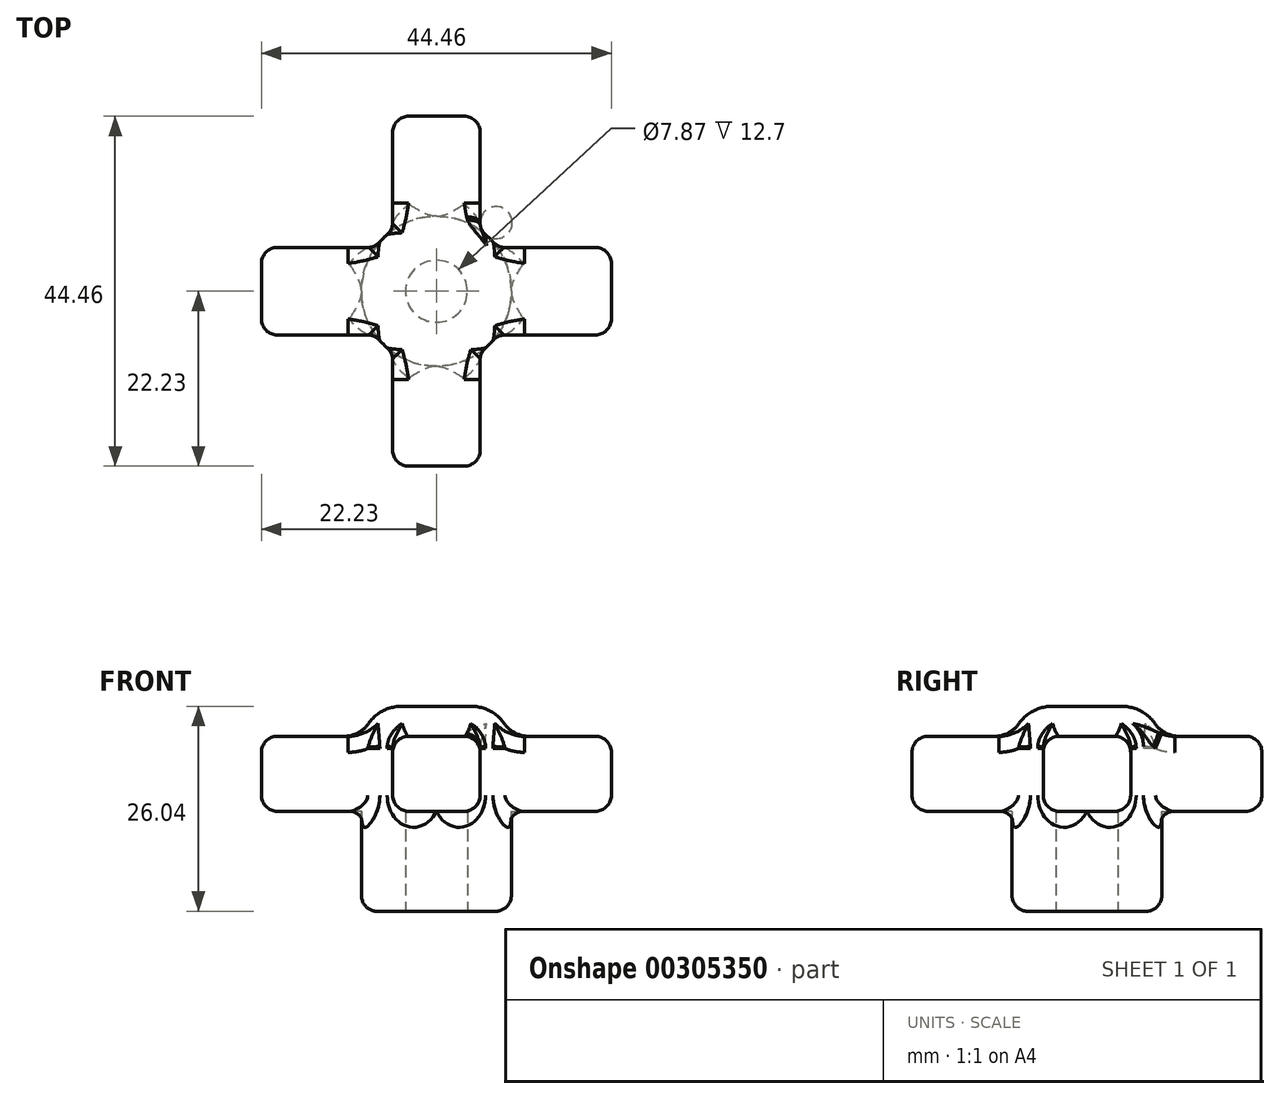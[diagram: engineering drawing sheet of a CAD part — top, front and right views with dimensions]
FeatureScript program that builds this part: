
annotation { "Feature Type Name" : "Feature", "Feature Type Description" : "" }
export const myFeature = defineFeature(function(context is Context, id is Id, definition is map)
    precondition{}
    {
        {
            var Q0;
            Q0=qCreatedBy(makeId("Top.planeOp"),FACE);
            var sketch = newSketch(context, id + "F0", { "sketchPlane" : qUnion([Q0])});
            skCircle(sketch, "E0", {"center": v(0, 0) * mm, "radius": 9.53 * mm});
            skSolve(sketch);
        }
        {
            var Q0;
            Q0=makeQuery(id+"F0.imprint","IMPRINT",FACE,{"disambiguationData":[TD([[makeQuery(id+"F0.imprint","IMPRINT",EDGE,{"derivedFrom":sQuery(id+"F0.wireOp",EDGE,"E0")}),1.0]])]});
            extrude(context, id + "F1", {"entities" : qUnion([Q0]), "depth" : 12.7 * mm});
        }
        {
            var Q0;
            Q0=makeQuery(id+"F1.opExtrude","CAP_FACE",FACE,{"disambiguationData":[OSD([sQuery(id+"F0.wireOp",EDGE,"E0")])],"isStart":false});
            var sketch = newSketch(context, id + "F2", { "sketchPlane" : qUnion([Q0])});
            skLineSegment(sketch, "E1.bottom", {"start": v(-5.56, 22.23) * mm, "end": v(5.56, 22.23) * mm});
            skLineSegment(sketch, "E1.top", {"start": v(-5.56, -22.23) * mm, "end": v(5.56, -22.23) * mm});
            skLineSegment(sketch, "E1.left", {"start": v(-5.56, 22.23) * mm, "end": v(-5.56, -22.23) * mm});
            skLineSegment(sketch, "E1.right", {"start": v(5.56, 22.23) * mm, "end": v(5.56, -22.23) * mm});
            skPoint(sketch, "E1.middle", {"position": v(0, 0) * mm});
            skLineSegment(sketch, "E2.bottom", {"start": v(22.23, 5.56) * mm, "end": v(-22.23, 5.56) * mm});
            skLineSegment(sketch, "E2.top", {"start": v(22.23, -5.56) * mm, "end": v(-22.23, -5.56) * mm});
            skLineSegment(sketch, "E2.left", {"start": v(22.23, 5.56) * mm, "end": v(22.23, -5.56) * mm});
            skLineSegment(sketch, "E2.right", {"start": v(-22.23, 5.56) * mm, "end": v(-22.23, -5.56) * mm});
            skSolve(sketch);
        }
        {
            var Q0;
            {var subQ0=sQuery(id+"F2.wireOp",EDGE,"E1.bottom");Q0=makeQuery(id+"F2.imprint","IMPRINT",FACE,{"disambiguationData":[TD([[makeQuery(id+"F2.imprint","IMPRINT",EDGE,{"derivedFrom":subQ0}),-1.0]])]});}
            var Q1;
            {var subQ0=sQuery(id+"F2.wireOp",EDGE,"E2.left");Q1=makeQuery(id+"F2.imprint","IMPRINT",FACE,{"disambiguationData":[TD([[makeQuery(id+"F2.imprint","IMPRINT",EDGE,{"derivedFrom":subQ0}),-1.0]])]});}
            var Q2;
            {var subQ0=sQuery(id+"F2.wireOp",EDGE,"E2.bottom");var subQ1=sQuery(id+"F2.wireOp",EDGE,"E1.left");var subQ2=makeQuery(id+"F2.imprint","INTERSECT",VERTEX,{"derivedFrom":[subQ1,subQ0]});Q2=makeQuery(id+"F2.imprint","IMPRINT",FACE,{"disambiguationData":[TD([[makeQuery(id+"F2.imprint","IMPRINT",EDGE,{"disambiguationData":[TD([[subQ2,-1.0]])],"derivedFrom":subQ1}),1.0]])]});}
            var Q3;
            {var subQ0=sQuery(id+"F2.wireOp",EDGE,"E2.bottom");var subQ1=sQuery(id+"F2.wireOp",EDGE,"E1.left");var subQ2=makeQuery(id+"F2.imprint","INTERSECT",VERTEX,{"derivedFrom":[subQ1,subQ0]});Q3=makeQuery(id+"F2.imprint","IMPRINT",FACE,{"disambiguationData":[TD([[makeQuery(id+"F2.imprint","IMPRINT",EDGE,{"disambiguationData":[TD([[subQ2,1.0]])],"derivedFrom":subQ1}),1.0]])]});}
            var Q4;
            {var subQ0=sQuery(id+"F2.wireOp",EDGE,"E2.bottom");var subQ1=sQuery(id+"F2.wireOp",EDGE,"E1.right");var subQ2=makeQuery(id+"F2.imprint","INTERSECT",VERTEX,{"derivedFrom":[subQ1,subQ0]});Q4=makeQuery(id+"F2.imprint","IMPRINT",FACE,{"disambiguationData":[TD([[makeQuery(id+"F2.imprint","IMPRINT",EDGE,{"disambiguationData":[TD([[subQ2,-1.0]])],"derivedFrom":subQ1}),1.0]])]});}
            var Q5;
            {var subQ0=sQuery(id+"F2.wireOp",EDGE,"E2.top");var subQ1=sQuery(id+"F2.wireOp",EDGE,"E1.left");var subQ2=makeQuery(id+"F2.imprint","INTERSECT",VERTEX,{"derivedFrom":[subQ1,subQ0]});Q5=makeQuery(id+"F2.imprint","IMPRINT",FACE,{"disambiguationData":[TD([[makeQuery(id+"F2.imprint","IMPRINT",EDGE,{"disambiguationData":[TD([[subQ2,-1.0]])],"derivedFrom":subQ1}),1.0]])]});}
            var Q6;
            {var subQ0=sQuery(id+"F2.wireOp",EDGE,"E1.top");Q6=makeQuery(id+"F2.imprint","IMPRINT",FACE,{"disambiguationData":[TD([[makeQuery(id+"F2.imprint","IMPRINT",EDGE,{"derivedFrom":subQ0}),1.0]])]});}
            var Q7;
            {var subQ0=sQuery(id+"F2.wireOp",EDGE,"E2.right");Q7=makeQuery(id+"F2.imprint","IMPRINT",FACE,{"disambiguationData":[TD([[makeQuery(id+"F2.imprint","IMPRINT",EDGE,{"derivedFrom":subQ0}),1.0]])]});}
            var Q8;
            {var subQ0=sQuery(id+"F2.wireOp",EDGE,"E2.bottom");var subQ1=sQuery(id+"F2.wireOp",EDGE,"E1.left");var subQ2=makeQuery(id+"F2.imprint","INTERSECT",VERTEX,{"derivedFrom":[subQ1,subQ0]});Q8=makeQuery(id+"F2.imprint","IMPRINT",FACE,{"disambiguationData":[TD([[makeQuery(id+"F2.imprint","IMPRINT",EDGE,{"disambiguationData":[TD([[subQ2,-1.0]])],"derivedFrom":subQ1}),-1.0]])]});}
            var Q9;
            {var subQ0=sQuery(id+"F2.wireOp",EDGE,"E2.top");var subQ1=sQuery(id+"F2.wireOp",EDGE,"E1.right");var subQ2=makeQuery(id+"F2.imprint","INTERSECT",VERTEX,{"derivedFrom":[subQ1,subQ0]});Q9=makeQuery(id+"F2.imprint","IMPRINT",FACE,{"disambiguationData":[TD([[makeQuery(id+"F2.imprint","IMPRINT",EDGE,{"disambiguationData":[TD([[subQ2,-1.0]])],"derivedFrom":subQ1}),1.0]])]});}
            var Q10;
            {var subQ0=sQuery(id+"F2.wireOp",EDGE,"E2.top");var subQ1=sQuery(id+"F2.wireOp",EDGE,"E1.left");var subQ2=makeQuery(id+"F2.imprint","INTERSECT",VERTEX,{"derivedFrom":[subQ1,subQ0]});Q10=makeQuery(id+"F2.imprint","IMPRINT",FACE,{"disambiguationData":[TD([[makeQuery(id+"F2.imprint","IMPRINT",EDGE,{"disambiguationData":[TD([[subQ2,-1.0]])],"derivedFrom":subQ1}),-1.0]])]});}
            var Q11;
            {var subQ0=sQuery(id+"F2.wireOp",EDGE,"E2.bottom");var subQ1=sQuery(id+"F2.wireOp",EDGE,"E1.right");var subQ2=makeQuery(id+"F2.imprint","INTERSECT",VERTEX,{"derivedFrom":[subQ1,subQ0]});Q11=makeQuery(id+"F2.imprint","IMPRINT",FACE,{"disambiguationData":[TD([[makeQuery(id+"F2.imprint","IMPRINT",EDGE,{"disambiguationData":[TD([[subQ2,1.0]])],"derivedFrom":subQ1}),1.0]])]});}
            var Q12;
            {var subQ0=sQuery(id+"F2.wireOp",EDGE,"E2.bottom");var subQ1=sQuery(id+"F2.wireOp",EDGE,"E1.left");var subQ2=makeQuery(id+"F2.imprint","INTERSECT",VERTEX,{"derivedFrom":[subQ1,subQ0]});Q12=makeQuery(id+"F2.imprint","IMPRINT",FACE,{"disambiguationData":[TD([[makeQuery(id+"F2.imprint","IMPRINT",EDGE,{"disambiguationData":[TD([[subQ2,1.0]])],"derivedFrom":subQ1}),-1.0]])]});}
            extrude(context, id + "F3", {"entities" : qUnion([Q0, Q1, Q2, Q3, Q4, Q5, Q6, Q7, Q8, Q9, Q10, Q11, Q12]), "operationType" : NewBodyOperationType.ADD, "depth" : 9.52 * mm});
        }
        {
            var Q0;
            Q0=makeQuery(id+"F3.opExtrude","CAP_FACE",FACE,{"disambiguationData":[OSD([sQuery(id+"F0.wireOp",EDGE,"E0"),sQuery(id+"F2.wireOp",EDGE,"E1.bottom"),sQuery(id+"F2.wireOp",EDGE,"E1.top"),sQuery(id+"F2.wireOp",EDGE,"E1.left"),sQuery(id+"F2.wireOp",EDGE,"E1.right"),sQuery(id+"F2.wireOp",EDGE,"E2.bottom"),sQuery(id+"F2.wireOp",EDGE,"E2.top"),sQuery(id+"F2.wireOp",EDGE,"E2.left"),sQuery(id+"F2.wireOp",EDGE,"E2.right")])],"isStart":false});
            var sketch = newSketch(context, id + "F4", { "sketchPlane" : qUnion([Q0])});
            skCircle(sketch, "E3", {"center": v(0, 0) * mm, "radius": 9.53 * mm});
            skSolve(sketch);
        }
        {
            var Q0;
            Q0=makeQuery(id+"F4.imprint","IMPRINT",FACE,{"disambiguationData":[TD([[makeQuery(id+"F4.imprint","IMPRINT",EDGE,{"derivedFrom":sQuery(id+"F4.wireOp",EDGE,"E3")}),1.0]])]});
            extrude(context, id + "F5", {"entities" : qUnion([Q0]), "operationType" : NewBodyOperationType.ADD, "depth" : 3.8 * mm});
        }
        {
            var Q0;
            Q0=makeQuery(id+"F5.opExtrude","CAP_EDGE",EDGE,{"disambiguationData":[OSD([sQuery(id+"F4.wireOp",EDGE,"E3")])],"isStart":false});
            fillet(context, id + "F6", {"entities" : qUnion([Q0]), "radius" : 5.08 * mm, "tangentPropagation" : true, "allowEdgeOverflow" : false});
        }
        {
            var Q0;
            {var subQ0=sQuery(id+"F2.wireOp",EDGE,"E2.left");var subQ1=sQuery(id+"F2.wireOp",EDGE,"E2.top");var subQ2=sQuery(id+"F0.wireOp",EDGE,"E0");var subQ5=sQuery(id+"F2.wireOp",EDGE,"E2.bottom");var subQ7=sQuery(id+"F2.wireOp",EDGE,"E1.left");var subQ8=sQuery(id+"F2.wireOp",EDGE,"E1.right");var subQ9=sQuery(id+"F4.wireOp",EDGE,"E3");Q0=makeQuery(id+"F6.opFillet","BLEND_EDGE",EDGE,{"blendedFrom":[makeQuery(id+"F5.opExtrude","CAP_EDGE",EDGE,{"disambiguationData":[OSD([subQ9])],"isStart":false}),makeQuery(id+"F5.boolean.opBoolean","SPLIT",FACE,{"disambiguationData":[TD([makeQuery(id+"F3.opExtrude","SWEPT_FACE",FACE,{"disambiguationData":[OSD([subQ0])]})])],"derivedFrom":makeQuery(id+"F3.opExtrude","CAP_FACE",FACE,{"disambiguationData":[OSD([subQ2,sQuery(id+"F2.wireOp",EDGE,"E1.bottom"),sQuery(id+"F2.wireOp",EDGE,"E1.top"),subQ7,subQ8,subQ5,subQ1,subQ0,sQuery(id+"F2.wireOp",EDGE,"E2.right")])],"isStart":false})})],"blendedInto":[makeQuery(id+"F5.boolean.opBoolean","SPLIT",FACE,{"disambiguationData":[TD([makeQuery(id+"F3.opExtrude","SWEPT_FACE",FACE,{"disambiguationData":[OSD([subQ0])]})])],"derivedFrom":makeQuery(id+"F3.opExtrude","CAP_FACE",FACE,{"disambiguationData":[OSD([subQ2,sQuery(id+"F2.wireOp",EDGE,"E1.bottom"),sQuery(id+"F2.wireOp",EDGE,"E1.top"),subQ7,subQ8,subQ5,subQ1,subQ0,sQuery(id+"F2.wireOp",EDGE,"E2.right")])],"isStart":false})})]});}
            var Q1;
            {var subQ0=sQuery(id+"F2.wireOp",EDGE,"E1.right");var subQ1=sQuery(id+"F2.wireOp",EDGE,"E1.bottom");var subQ2=sQuery(id+"F0.wireOp",EDGE,"E0");var subQ5=sQuery(id+"F2.wireOp",EDGE,"E2.top");var subQ6=sQuery(id+"F2.wireOp",EDGE,"E1.left");var subQ8=sQuery(id+"F2.wireOp",EDGE,"E2.bottom");var subQ9=sQuery(id+"F4.wireOp",EDGE,"E3");Q1=makeQuery(id+"F6.opFillet","BLEND_EDGE",EDGE,{"blendedFrom":[makeQuery(id+"F5.opExtrude","CAP_EDGE",EDGE,{"disambiguationData":[OSD([subQ9])],"isStart":false}),makeQuery(id+"F5.boolean.opBoolean","SPLIT",FACE,{"disambiguationData":[TD([makeQuery(id+"F3.opExtrude","SWEPT_FACE",FACE,{"disambiguationData":[OSD([subQ1])]})])],"derivedFrom":makeQuery(id+"F3.opExtrude","CAP_FACE",FACE,{"disambiguationData":[OSD([subQ2,subQ1,sQuery(id+"F2.wireOp",EDGE,"E1.top"),subQ6,subQ0,subQ8,subQ5,sQuery(id+"F2.wireOp",EDGE,"E2.left"),sQuery(id+"F2.wireOp",EDGE,"E2.right")])],"isStart":false})})],"blendedInto":[makeQuery(id+"F5.boolean.opBoolean","SPLIT",FACE,{"disambiguationData":[TD([makeQuery(id+"F3.opExtrude","SWEPT_FACE",FACE,{"disambiguationData":[OSD([subQ1])]})])],"derivedFrom":makeQuery(id+"F3.opExtrude","CAP_FACE",FACE,{"disambiguationData":[OSD([subQ2,subQ1,sQuery(id+"F2.wireOp",EDGE,"E1.top"),subQ6,subQ0,subQ8,subQ5,sQuery(id+"F2.wireOp",EDGE,"E2.left"),sQuery(id+"F2.wireOp",EDGE,"E2.right")])],"isStart":false})})]});}
            var Q2;
            {var subQ0=sQuery(id+"F2.wireOp",EDGE,"E2.right");var subQ1=sQuery(id+"F2.wireOp",EDGE,"E2.top");var subQ2=sQuery(id+"F0.wireOp",EDGE,"E0");var subQ5=sQuery(id+"F2.wireOp",EDGE,"E2.bottom");var subQ7=sQuery(id+"F2.wireOp",EDGE,"E1.left");var subQ8=sQuery(id+"F2.wireOp",EDGE,"E1.right");var subQ9=sQuery(id+"F4.wireOp",EDGE,"E3");Q2=makeQuery(id+"F6.opFillet","BLEND_EDGE",EDGE,{"blendedFrom":[makeQuery(id+"F5.opExtrude","CAP_EDGE",EDGE,{"disambiguationData":[OSD([subQ9])],"isStart":false}),makeQuery(id+"F5.boolean.opBoolean","SPLIT",FACE,{"disambiguationData":[TD([makeQuery(id+"F3.opExtrude","SWEPT_FACE",FACE,{"disambiguationData":[OSD([subQ0])]})])],"derivedFrom":makeQuery(id+"F3.opExtrude","CAP_FACE",FACE,{"disambiguationData":[OSD([subQ2,sQuery(id+"F2.wireOp",EDGE,"E1.bottom"),sQuery(id+"F2.wireOp",EDGE,"E1.top"),subQ7,subQ8,subQ5,subQ1,sQuery(id+"F2.wireOp",EDGE,"E2.left"),subQ0])],"isStart":false})})],"blendedInto":[makeQuery(id+"F5.boolean.opBoolean","SPLIT",FACE,{"disambiguationData":[TD([makeQuery(id+"F3.opExtrude","SWEPT_FACE",FACE,{"disambiguationData":[OSD([subQ0])]})])],"derivedFrom":makeQuery(id+"F3.opExtrude","CAP_FACE",FACE,{"disambiguationData":[OSD([subQ2,sQuery(id+"F2.wireOp",EDGE,"E1.bottom"),sQuery(id+"F2.wireOp",EDGE,"E1.top"),subQ7,subQ8,subQ5,subQ1,sQuery(id+"F2.wireOp",EDGE,"E2.left"),subQ0])],"isStart":false})})]});}
            var Q3;
            {var subQ0=sQuery(id+"F2.wireOp",EDGE,"E1.left");var subQ1=sQuery(id+"F2.wireOp",EDGE,"E1.top");var subQ2=sQuery(id+"F0.wireOp",EDGE,"E0");var subQ5=sQuery(id+"F2.wireOp",EDGE,"E1.right");var subQ6=sQuery(id+"F2.wireOp",EDGE,"E2.bottom");var subQ7=sQuery(id+"F4.wireOp",EDGE,"E3");var subQ9=sQuery(id+"F2.wireOp",EDGE,"E2.top");Q3=makeQuery(id+"F6.opFillet","BLEND_EDGE",EDGE,{"blendedFrom":[makeQuery(id+"F5.opExtrude","CAP_EDGE",EDGE,{"disambiguationData":[OSD([subQ7])],"isStart":false}),makeQuery(id+"F5.boolean.opBoolean","SPLIT",FACE,{"disambiguationData":[TD([makeQuery(id+"F3.opExtrude","SWEPT_FACE",FACE,{"disambiguationData":[OSD([subQ1])]})])],"derivedFrom":makeQuery(id+"F3.opExtrude","CAP_FACE",FACE,{"disambiguationData":[OSD([subQ2,sQuery(id+"F2.wireOp",EDGE,"E1.bottom"),subQ1,subQ0,subQ5,subQ6,subQ9,sQuery(id+"F2.wireOp",EDGE,"E2.left"),sQuery(id+"F2.wireOp",EDGE,"E2.right")])],"isStart":false})})],"blendedInto":[makeQuery(id+"F5.boolean.opBoolean","SPLIT",FACE,{"disambiguationData":[TD([makeQuery(id+"F3.opExtrude","SWEPT_FACE",FACE,{"disambiguationData":[OSD([subQ1])]})])],"derivedFrom":makeQuery(id+"F3.opExtrude","CAP_FACE",FACE,{"disambiguationData":[OSD([subQ2,sQuery(id+"F2.wireOp",EDGE,"E1.bottom"),subQ1,subQ0,subQ5,subQ6,subQ9,sQuery(id+"F2.wireOp",EDGE,"E2.left"),sQuery(id+"F2.wireOp",EDGE,"E2.right")])],"isStart":false})})]});}
            fillet(context, id + "F7", {"entities" : qUnion([Q0, Q1, Q2, Q3]), "radius" : 3.8 * mm, "tangentPropagation" : true, "allowEdgeOverflow" : false});
        }
        {
            var Q0;
            Q0=makeQuery(id+"F3.opExtrude","CAP_EDGE",EDGE,{"disambiguationData":[OSD([sQuery(id+"F2.wireOp",EDGE,"E2.left")])],"isStart":false});
            var Q1;
            {var subQ0=sQuery(id+"F2.wireOp",EDGE,"E2.bottom");Q1=makeQuery(id+"F3.opExtrude","CAP_EDGE",EDGE,{"disambiguationData":[OSD([subQ0]),TDD([makeQuery(id+"F2.imprint","IMPRINT",EDGE,{"disambiguationData":[TD([[makeQuery(id+"F2.imprint","INTERSECT",VERTEX,{"derivedFrom":[subQ0,sQuery(id+"F2.wireOp",EDGE,"E2.left")]}),-1.0]])],"derivedFrom":subQ0})])],"isStart":false});}
            var Q2;
            {var subQ0=sQuery(id+"F2.wireOp",EDGE,"E2.top");Q2=makeQuery(id+"F3.opExtrude","CAP_EDGE",EDGE,{"disambiguationData":[OSD([subQ0]),TDD([makeQuery(id+"F2.imprint","IMPRINT",EDGE,{"disambiguationData":[TD([[makeQuery(id+"F2.imprint","INTERSECT",VERTEX,{"derivedFrom":[subQ0,sQuery(id+"F2.wireOp",EDGE,"E2.left")]}),-1.0]])],"derivedFrom":subQ0})])],"isStart":false});}
            var Q3;
            {var subQ0=sQuery(id+"F2.wireOp",EDGE,"E2.top");Q3=makeQuery(id+"F3.opExtrude","CAP_EDGE",EDGE,{"disambiguationData":[OSD([subQ0]),TDD([makeQuery(id+"F2.imprint","IMPRINT",EDGE,{"disambiguationData":[TD([[makeQuery(id+"F2.imprint","INTERSECT",VERTEX,{"derivedFrom":[subQ0,sQuery(id+"F2.wireOp",EDGE,"E2.left")]}),-1.0]])],"derivedFrom":subQ0})])],"isStart":true});}
            var Q4;
            Q4=makeQuery(id+"F3.opExtrude","CAP_EDGE",EDGE,{"disambiguationData":[OSD([sQuery(id+"F2.wireOp",EDGE,"E2.left")])],"isStart":true});
            var Q5;
            Q5=makeQuery(id+"F3.opExtrude","SWEPT_EDGE",EDGE,{"disambiguationData":[OSD([sQuery(id+"F2.wireOp",EDGE,"E2.top"),sQuery(id+"F2.wireOp",EDGE,"E2.left")])]});
            var Q6;
            Q6=makeQuery(id+"F3.opExtrude","SWEPT_EDGE",EDGE,{"disambiguationData":[OSD([sQuery(id+"F2.wireOp",EDGE,"E2.bottom"),sQuery(id+"F2.wireOp",EDGE,"E2.left")])]});
            var Q7;
            {var subQ0=sQuery(id+"F2.wireOp",EDGE,"E2.bottom");Q7=makeQuery(id+"F3.opExtrude","CAP_EDGE",EDGE,{"disambiguationData":[OSD([subQ0]),TDD([makeQuery(id+"F2.imprint","IMPRINT",EDGE,{"disambiguationData":[TD([[makeQuery(id+"F2.imprint","INTERSECT",VERTEX,{"derivedFrom":[subQ0,sQuery(id+"F2.wireOp",EDGE,"E2.left")]}),-1.0]])],"derivedFrom":subQ0})])],"isStart":true});}
            var Q8;
            {var subQ0=sQuery(id+"F2.wireOp",EDGE,"E1.right");Q8=makeQuery(id+"F3.opExtrude","CAP_EDGE",EDGE,{"disambiguationData":[OSD([subQ0]),TDD([makeQuery(id+"F2.imprint","IMPRINT",EDGE,{"disambiguationData":[TD([[makeQuery(id+"F2.imprint","INTERSECT",VERTEX,{"derivedFrom":[sQuery(id+"F2.wireOp",EDGE,"E1.bottom"),subQ0]}),-1.0]])],"derivedFrom":subQ0})])],"isStart":true});}
            var Q9;
            Q9=makeQuery(id+"F3.opExtrude","SWEPT_EDGE",EDGE,{"disambiguationData":[OSD([sQuery(id+"F2.wireOp",EDGE,"E1.bottom"),sQuery(id+"F2.wireOp",EDGE,"E1.right")])]});
            var Q10;
            Q10=makeQuery(id+"F3.opExtrude","CAP_EDGE",EDGE,{"disambiguationData":[OSD([sQuery(id+"F2.wireOp",EDGE,"E1.bottom")])],"isStart":false});
            var Q11;
            Q11=makeQuery(id+"F3.opExtrude","CAP_EDGE",EDGE,{"disambiguationData":[OSD([sQuery(id+"F2.wireOp",EDGE,"E1.bottom")])],"isStart":true});
            var Q12;
            Q12=makeQuery(id+"F3.opExtrude","SWEPT_EDGE",EDGE,{"disambiguationData":[OSD([sQuery(id+"F2.wireOp",EDGE,"E1.bottom"),sQuery(id+"F2.wireOp",EDGE,"E1.left")])]});
            var Q13;
            {var subQ0=sQuery(id+"F2.wireOp",EDGE,"E1.left");Q13=makeQuery(id+"F3.opExtrude","CAP_EDGE",EDGE,{"disambiguationData":[OSD([subQ0]),TDD([makeQuery(id+"F2.imprint","IMPRINT",EDGE,{"disambiguationData":[TD([[makeQuery(id+"F2.imprint","INTERSECT",VERTEX,{"derivedFrom":[sQuery(id+"F2.wireOp",EDGE,"E1.bottom"),subQ0]}),-1.0]])],"derivedFrom":subQ0})])],"isStart":false});}
            var Q14;
            {var subQ0=sQuery(id+"F2.wireOp",EDGE,"E1.left");Q14=makeQuery(id+"F3.opExtrude","CAP_EDGE",EDGE,{"disambiguationData":[OSD([subQ0]),TDD([makeQuery(id+"F2.imprint","IMPRINT",EDGE,{"disambiguationData":[TD([[makeQuery(id+"F2.imprint","INTERSECT",VERTEX,{"derivedFrom":[sQuery(id+"F2.wireOp",EDGE,"E1.bottom"),subQ0]}),-1.0]])],"derivedFrom":subQ0})])],"isStart":true});}
            var Q15;
            {var subQ0=sQuery(id+"F2.wireOp",EDGE,"E2.bottom");Q15=makeQuery(id+"F3.opExtrude","CAP_EDGE",EDGE,{"disambiguationData":[OSD([subQ0]),TDD([makeQuery(id+"F2.imprint","IMPRINT",EDGE,{"disambiguationData":[TD([[makeQuery(id+"F2.imprint","INTERSECT",VERTEX,{"derivedFrom":[subQ0,sQuery(id+"F2.wireOp",EDGE,"E2.right")]}),1.0]])],"derivedFrom":subQ0})])],"isStart":false});}
            var Q16;
            Q16=makeQuery(id+"F3.opExtrude","SWEPT_EDGE",EDGE,{"disambiguationData":[OSD([sQuery(id+"F2.wireOp",EDGE,"E2.bottom"),sQuery(id+"F2.wireOp",EDGE,"E2.right")])]});
            var Q17;
            {var subQ0=sQuery(id+"F2.wireOp",EDGE,"E2.bottom");Q17=makeQuery(id+"F3.opExtrude","CAP_EDGE",EDGE,{"disambiguationData":[OSD([subQ0]),TDD([makeQuery(id+"F2.imprint","IMPRINT",EDGE,{"disambiguationData":[TD([[makeQuery(id+"F2.imprint","INTERSECT",VERTEX,{"derivedFrom":[subQ0,sQuery(id+"F2.wireOp",EDGE,"E2.right")]}),1.0]])],"derivedFrom":subQ0})])],"isStart":true});}
            var Q18;
            Q18=makeQuery(id+"F3.opExtrude","CAP_EDGE",EDGE,{"disambiguationData":[OSD([sQuery(id+"F2.wireOp",EDGE,"E2.right")])],"isStart":true});
            var Q19;
            Q19=makeQuery(id+"F3.opExtrude","CAP_EDGE",EDGE,{"disambiguationData":[OSD([sQuery(id+"F2.wireOp",EDGE,"E2.right")])],"isStart":false});
            var Q20;
            {var subQ0=sQuery(id+"F2.wireOp",EDGE,"E2.top");Q20=makeQuery(id+"F3.opExtrude","CAP_EDGE",EDGE,{"disambiguationData":[OSD([subQ0]),TDD([makeQuery(id+"F2.imprint","IMPRINT",EDGE,{"disambiguationData":[TD([[makeQuery(id+"F2.imprint","INTERSECT",VERTEX,{"derivedFrom":[subQ0,sQuery(id+"F2.wireOp",EDGE,"E2.right")]}),1.0]])],"derivedFrom":subQ0})])],"isStart":false});}
            var Q21;
            Q21=makeQuery(id+"F3.opExtrude","SWEPT_EDGE",EDGE,{"disambiguationData":[OSD([sQuery(id+"F2.wireOp",EDGE,"E2.top"),sQuery(id+"F2.wireOp",EDGE,"E2.right")])]});
            var Q22;
            {var subQ0=sQuery(id+"F2.wireOp",EDGE,"E2.top");Q22=makeQuery(id+"F3.opExtrude","CAP_EDGE",EDGE,{"disambiguationData":[OSD([subQ0]),TDD([makeQuery(id+"F2.imprint","IMPRINT",EDGE,{"disambiguationData":[TD([[makeQuery(id+"F2.imprint","INTERSECT",VERTEX,{"derivedFrom":[subQ0,sQuery(id+"F2.wireOp",EDGE,"E2.right")]}),1.0]])],"derivedFrom":subQ0})])],"isStart":true});}
            var Q23;
            Q23=makeQuery(id+"F3.opExtrude","SWEPT_EDGE",EDGE,{"disambiguationData":[OSD([sQuery(id+"F2.wireOp",EDGE,"E1.top"),sQuery(id+"F2.wireOp",EDGE,"E1.left")])]});
            var Q24;
            {var subQ0=sQuery(id+"F2.wireOp",EDGE,"E1.left");Q24=makeQuery(id+"F3.opExtrude","CAP_EDGE",EDGE,{"disambiguationData":[OSD([subQ0]),TDD([makeQuery(id+"F2.imprint","IMPRINT",EDGE,{"disambiguationData":[TD([[makeQuery(id+"F2.imprint","INTERSECT",VERTEX,{"derivedFrom":[sQuery(id+"F2.wireOp",EDGE,"E1.top"),subQ0]}),1.0]])],"derivedFrom":subQ0})])],"isStart":true});}
            var Q25;
            {var subQ0=sQuery(id+"F2.wireOp",EDGE,"E1.left");Q25=makeQuery(id+"F3.opExtrude","CAP_EDGE",EDGE,{"disambiguationData":[OSD([subQ0]),TDD([makeQuery(id+"F2.imprint","IMPRINT",EDGE,{"disambiguationData":[TD([[makeQuery(id+"F2.imprint","INTERSECT",VERTEX,{"derivedFrom":[sQuery(id+"F2.wireOp",EDGE,"E1.top"),subQ0]}),1.0]])],"derivedFrom":subQ0})])],"isStart":false});}
            var Q26;
            Q26=makeQuery(id+"F3.opExtrude","CAP_EDGE",EDGE,{"disambiguationData":[OSD([sQuery(id+"F2.wireOp",EDGE,"E1.top")])],"isStart":false});
            var Q27;
            Q27=makeQuery(id+"F3.opExtrude","CAP_EDGE",EDGE,{"disambiguationData":[OSD([sQuery(id+"F2.wireOp",EDGE,"E1.top")])],"isStart":true});
            var Q28;
            {var subQ0=sQuery(id+"F2.wireOp",EDGE,"E1.right");Q28=makeQuery(id+"F3.opExtrude","CAP_EDGE",EDGE,{"disambiguationData":[OSD([subQ0]),TDD([makeQuery(id+"F2.imprint","IMPRINT",EDGE,{"disambiguationData":[TD([[makeQuery(id+"F2.imprint","INTERSECT",VERTEX,{"derivedFrom":[sQuery(id+"F2.wireOp",EDGE,"E1.top"),subQ0]}),1.0]])],"derivedFrom":subQ0})])],"isStart":false});}
            var Q29;
            Q29=makeQuery(id+"F3.opExtrude","SWEPT_EDGE",EDGE,{"disambiguationData":[OSD([sQuery(id+"F2.wireOp",EDGE,"E1.top"),sQuery(id+"F2.wireOp",EDGE,"E1.right")])]});
            var Q30;
            {var subQ0=sQuery(id+"F2.wireOp",EDGE,"E1.right");Q30=makeQuery(id+"F3.opExtrude","CAP_EDGE",EDGE,{"disambiguationData":[OSD([subQ0]),TDD([makeQuery(id+"F2.imprint","IMPRINT",EDGE,{"disambiguationData":[TD([[makeQuery(id+"F2.imprint","INTERSECT",VERTEX,{"derivedFrom":[sQuery(id+"F2.wireOp",EDGE,"E1.top"),subQ0]}),1.0]])],"derivedFrom":subQ0})])],"isStart":true});}
            var Q31;
            {var subQ0=sQuery(id+"F2.wireOp",EDGE,"E1.right");var subQ1=sQuery(id+"F0.wireOp",EDGE,"E0");Q31=makeQuery(id+"F3.opExtrude","SWEPT_EDGE",EDGE,{"disambiguationData":[OSD([subQ1,subQ0]),TDD([makeQuery(id+"F2.imprint","INTERSECT",VERTEX,{"disambiguationData":[OD(1.0)],"derivedFrom":[makeQuery(id+"F1.opExtrude","CAP_EDGE",EDGE,{"disambiguationData":[OSD([subQ1])],"isStart":false}),subQ0]})])]});}
            var Q32;
            {var subQ0=sQuery(id+"F2.wireOp",EDGE,"E2.top");var subQ1=sQuery(id+"F0.wireOp",EDGE,"E0");Q32=makeQuery(id+"F3.opExtrude","SWEPT_EDGE",EDGE,{"disambiguationData":[OSD([subQ1,subQ0]),TDD([makeQuery(id+"F2.imprint","INTERSECT",VERTEX,{"disambiguationData":[OD(0.0)],"derivedFrom":[makeQuery(id+"F1.opExtrude","CAP_EDGE",EDGE,{"disambiguationData":[OSD([subQ1])],"isStart":false}),subQ0]})])]});}
            var Q33;
            {var subQ0=sQuery(id+"F2.wireOp",EDGE,"E2.bottom");var subQ1=sQuery(id+"F0.wireOp",EDGE,"E0");Q33=makeQuery(id+"F3.opExtrude","SWEPT_EDGE",EDGE,{"disambiguationData":[OSD([subQ1,subQ0]),TDD([makeQuery(id+"F2.imprint","INTERSECT",VERTEX,{"disambiguationData":[OD(0.0)],"derivedFrom":[makeQuery(id+"F1.opExtrude","CAP_EDGE",EDGE,{"disambiguationData":[OSD([subQ1])],"isStart":false}),subQ0]})])]});}
            var Q34;
            {var subQ0=sQuery(id+"F2.wireOp",EDGE,"E1.right");var subQ1=sQuery(id+"F0.wireOp",EDGE,"E0");Q34=makeQuery(id+"F3.opExtrude","SWEPT_EDGE",EDGE,{"disambiguationData":[OSD([subQ1,subQ0]),TDD([makeQuery(id+"F2.imprint","INTERSECT",VERTEX,{"disambiguationData":[OD(0.0)],"derivedFrom":[makeQuery(id+"F1.opExtrude","CAP_EDGE",EDGE,{"disambiguationData":[OSD([subQ1])],"isStart":false}),subQ0]})])]});}
            var Q35;
            {var subQ0=sQuery(id+"F2.wireOp",EDGE,"E1.left");var subQ1=sQuery(id+"F0.wireOp",EDGE,"E0");Q35=makeQuery(id+"F3.opExtrude","SWEPT_EDGE",EDGE,{"disambiguationData":[OSD([subQ1,subQ0]),TDD([makeQuery(id+"F2.imprint","INTERSECT",VERTEX,{"disambiguationData":[OD(0.0)],"derivedFrom":[makeQuery(id+"F1.opExtrude","CAP_EDGE",EDGE,{"disambiguationData":[OSD([subQ1])],"isStart":false}),subQ0]})])]});}
            var Q36;
            {var subQ0=sQuery(id+"F2.wireOp",EDGE,"E2.bottom");var subQ1=sQuery(id+"F0.wireOp",EDGE,"E0");Q36=makeQuery(id+"F3.opExtrude","SWEPT_EDGE",EDGE,{"disambiguationData":[OSD([subQ1,subQ0]),TDD([makeQuery(id+"F2.imprint","INTERSECT",VERTEX,{"disambiguationData":[OD(1.0)],"derivedFrom":[makeQuery(id+"F1.opExtrude","CAP_EDGE",EDGE,{"disambiguationData":[OSD([subQ1])],"isStart":false}),subQ0]})])]});}
            var Q37;
            {var subQ0=sQuery(id+"F2.wireOp",EDGE,"E2.top");var subQ1=sQuery(id+"F0.wireOp",EDGE,"E0");Q37=makeQuery(id+"F3.opExtrude","SWEPT_EDGE",EDGE,{"disambiguationData":[OSD([subQ1,subQ0]),TDD([makeQuery(id+"F2.imprint","INTERSECT",VERTEX,{"disambiguationData":[OD(1.0)],"derivedFrom":[makeQuery(id+"F1.opExtrude","CAP_EDGE",EDGE,{"disambiguationData":[OSD([subQ1])],"isStart":false}),subQ0]})])]});}
            var Q38;
            {var subQ0=sQuery(id+"F2.wireOp",EDGE,"E1.left");var subQ1=sQuery(id+"F0.wireOp",EDGE,"E0");Q38=makeQuery(id+"F3.opExtrude","SWEPT_EDGE",EDGE,{"disambiguationData":[OSD([subQ1,subQ0]),TDD([makeQuery(id+"F2.imprint","INTERSECT",VERTEX,{"disambiguationData":[OD(1.0)],"derivedFrom":[makeQuery(id+"F1.opExtrude","CAP_EDGE",EDGE,{"disambiguationData":[OSD([subQ1])],"isStart":false}),subQ0]})])]});}
            fillet(context, id + "F8", {"entities" : qUnion([Q0, Q1, Q2, Q3, Q4, Q5, Q6, Q7, Q8, Q9, Q10, Q11, Q12, Q13, Q14, Q15, Q16, Q17, Q18, Q19, Q20, Q21, Q22, Q23, Q24, Q25, Q26, Q27, Q28, Q29, Q30, Q31, Q32, Q33, Q34, Q35, Q36, Q37, Q38]), "radius" : 2.03 * mm, "tangentPropagation" : true, "allowEdgeOverflow" : false});
        }
        {
            var Q0;
            {var subQ0=sQuery(id+"F2.wireOp",EDGE,"E1.right");Q0=makeQuery(id+"F3.opExtrude","CAP_EDGE",EDGE,{"disambiguationData":[OSD([subQ0]),TDD([makeQuery(id+"F2.imprint","IMPRINT",EDGE,{"disambiguationData":[TD([[makeQuery(id+"F2.imprint","INTERSECT",VERTEX,{"derivedFrom":[sQuery(id+"F2.wireOp",EDGE,"E1.bottom"),subQ0]}),-1.0]])],"derivedFrom":subQ0})])],"isStart":false});}
            fillet(context, id + "F9", {"entities" : qUnion([Q0]), "radius" : 2.03 * mm, "tangentPropagation" : true, "allowEdgeOverflow" : false});
        }
        {
            var Q0;
            Q0=makeQuery(id+"F1.opExtrude","CAP_FACE",FACE,{"disambiguationData":[OSD([sQuery(id+"F0.wireOp",EDGE,"E0")])],"isStart":true});
            var sketch = newSketch(context, id + "F10", { "sketchPlane" : qUnion([Q0])});
            skCircle(sketch, "E4", {"center": v(0, 0) * mm, "radius": 3.94 * mm});
            skSolve(sketch);
        }
        {
            var Q0;
            Q0=makeQuery(id+"F10.imprint","IMPRINT",FACE,{"disambiguationData":[TD([[makeQuery(id+"F10.imprint","IMPRINT",EDGE,{"derivedFrom":sQuery(id+"F10.wireOp",EDGE,"E4")}),1.0]])]});
            extrude(context, id + "F11", {"entities" : qUnion([Q0]), "operationType" : NewBodyOperationType.REMOVE, "oppositeDirection" : true, "depth" : 12.7 * mm});
        }
        {
            var Q0;
            Q0=makeQuery(id+"F11.boolean.opBoolean","COPY",EDGE,{"derivedFrom":makeQuery(id+"F11.opExtrude","CAP_EDGE",EDGE,{"disambiguationData":[OSD([sQuery(id+"F10.wireOp",EDGE,"E4")])],"isStart":true})});
            var Q1;
            Q1=makeQuery(id+"F1.opExtrude","CAP_EDGE",EDGE,{"disambiguationData":[OSD([sQuery(id+"F0.wireOp",EDGE,"E0")])],"isStart":true});
            fillet(context, id + "F12", {"entities" : qUnion([Q0, Q1]), "radius" : 2.03 * mm, "tangentPropagation" : true, "allowEdgeOverflow" : false});
        }
    });
